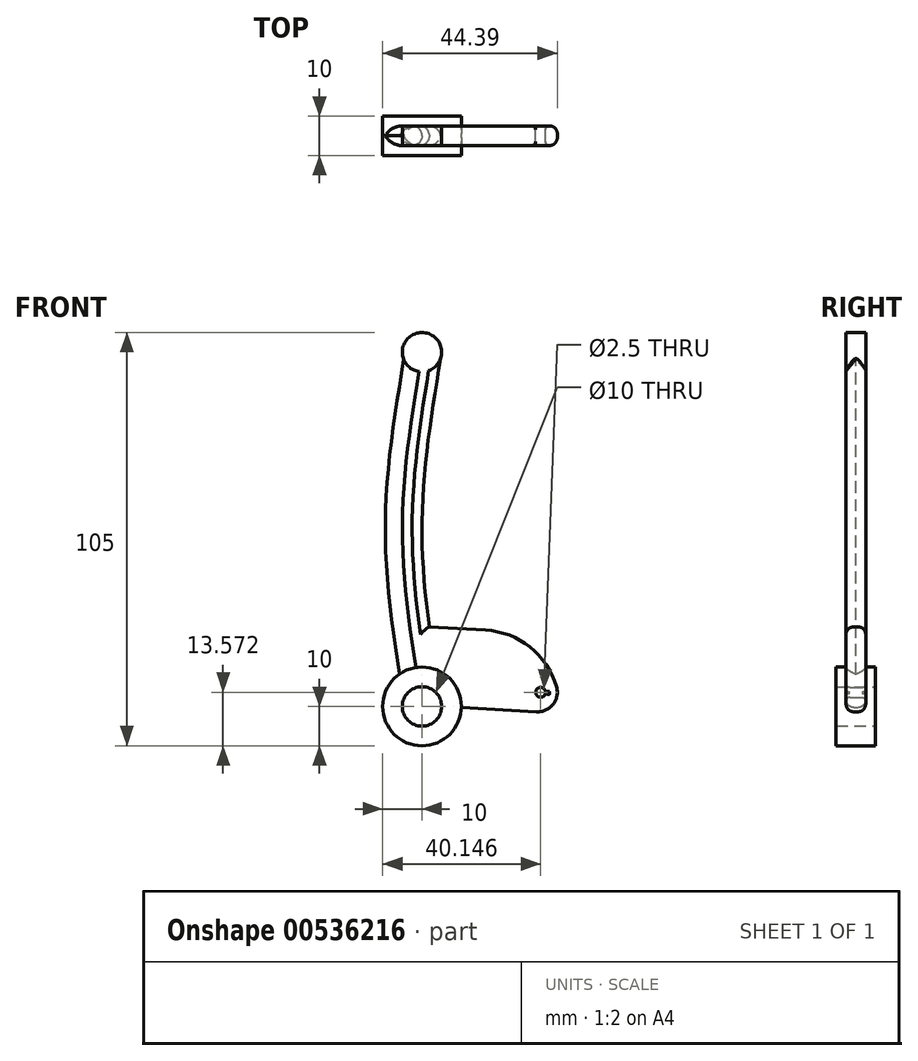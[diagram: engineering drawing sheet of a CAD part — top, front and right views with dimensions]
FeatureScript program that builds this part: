
annotation { "Feature Type Name" : "Feature", "Feature Type Description" : "" }
export const myFeature = defineFeature(function(context is Context, id is Id, definition is map)
    precondition{}
    {
        {
            var Q0;
            Q0=qCreatedBy(makeId("Front.planeOp"),FACE);
            var sketch = newSketch(context, id + "F0", { "sketchPlane" : qUnion([Q0])});
            skPoint(sketch, "E0.middle", {"position": v(0, 0) * mm});
            skFitSpline(sketch, "E1", {"points": [v(7.5, 45) * mm, v(2.5, 0) * mm, v(7.5, -45) * mm], "startDerivative": vector(-15, -90) * mm, "endDerivative": vector(15, -90) * mm});
            skFitSpline(sketch, "E2", {"points": [v(-2.5, -45) * mm, v(-7.5, 0) * mm, v(-2.5, 45) * mm], "startDerivative": vector(-15, 90) * mm, "endDerivative": vector(15, 90) * mm});
            skPoint(sketch, "E3.start.orphan", {"position": v(7.5, 0) * mm});
            skCircle(sketch, "E4", {"center": v(2.5, -45) * mm, "radius": 10 * mm});
            skCircle(sketch, "E5", {"center": v(2.5, -45) * mm, "radius": 5 * mm});
            skArc(sketch, "E6", {"start": v(7.23, 43.38) * mm, "mid": v(3.32, 49.93) * mm, "end": v(-2.5, 45) * mm});
            skLineSegment(sketch, "E7", {"start": v(7.5, -45) * mm, "end": v(37.45, -46.7) * mm});
            skLineSegment(sketch, "E8", {"start": v(37.45, -46.7) * mm, "end": v(38.59, -26.73) * mm});
            skLineSegment(sketch, "E9", {"start": v(38.59, -26.73) * mm, "end": v(4.36, -24.79) * mm});
            skCircle(sketch, "E10", {"center": v(32.65, -41.43) * mm, "radius": 1.25 * mm});
            skSolve(sketch);
        }
        {
            var Q0;
            Q0 = qSketchRegion(id + "F0", true);
            extrude(context, id + "F1", {"entities" : qUnion([Q0]), "depth" : 5 * mm, "offsetDistance" : 25 * mm, "symmetric" : true});
        }
        {
            var Q0;
            Q0=makeQuery(id+"F1.opExtrude","CAP_EDGE",EDGE,{"disambiguationData":[OSD([sQuery(id+"F0.wireOp",EDGE,"E2")])],"isStart":false});
            var Q1;
            Q1=makeQuery(id+"F1.opExtrude","CAP_EDGE",EDGE,{"disambiguationData":[OSD([sQuery(id+"F0.wireOp",EDGE,"E2")])],"isStart":true});
            fillet(context, id + "F2", {"entities" : qUnion([Q0, Q1]), "radius" : 5 * mm, "tangentPropagation" : true, "allowEdgeOverflow" : false});
        }
        {
            var Q0;
            Q0=makeQuery(id+"F1.opExtrude","CAP_EDGE",EDGE,{"disambiguationData":[OSD([sQuery(id+"F0.wireOp",EDGE,"E1")])],"isStart":false});
            var Q1;
            Q1=makeQuery(id+"F1.opExtrude","CAP_EDGE",EDGE,{"disambiguationData":[OSD([sQuery(id+"F0.wireOp",EDGE,"E1")])],"isStart":true});
            fillet(context, id + "F3", {"entities" : qUnion([Q0, Q1]), "radius" : 2.5 * mm, "tangentPropagation" : true, "allowEdgeOverflow" : false});
        }
        {
            var Q0;
            Q0=makeQuery(id+"F1.opExtrude","CAP_FACE",FACE,{"disambiguationData":[OSD([sQuery(id+"F0.wireOp",EDGE,"E1"),sQuery(id+"F0.wireOp",EDGE,"E2"),sQuery(id+"F0.wireOp",EDGE,"E4"),sQuery(id+"F0.wireOp",EDGE,"E5"),sQuery(id+"F0.wireOp",EDGE,"E6")])],"isStart":false});
            var sketch = newSketch(context, id + "F4", { "sketchPlane" : qUnion([Q0])});
            skCircle(sketch, "E11", {"center": v(2.5, -45) * mm, "radius": 10 * mm});
            skSolve(sketch);
        }
        {
            var Q0;
            Q0 = qSketchRegion(id + "F4", true);
            extrude(context, id + "F5", {"entities" : qUnion([Q0]), "operationType" : NewBodyOperationType.ADD, "depth" : 2.5 * mm, "offsetDistance" : 25 * mm});
        }
        {
            var Q0;
            Q0=makeQuery(id+"F5.opExtrude","CAP_FACE",FACE,{"disambiguationData":[OSD([sQuery(id+"F4.wireOp",EDGE,"E11")])],"isStart":true});
            extrude(context, id + "F6", {"entities" : qUnion([Q0]), "operationType" : NewBodyOperationType.REMOVE, "oppositeDirection" : true, "depth" : 25 * mm, "offsetDistance" : 25 * mm});
        }
        {
            var Q0;
            Q0=makeQuery(id+"F5.opExtrude","CAP_FACE",FACE,{"disambiguationData":[OSD([sQuery(id+"F4.wireOp",EDGE,"E11")])],"isStart":false});
            extrude(context, id + "F7", {"entities" : qUnion([Q0]), "operationType" : NewBodyOperationType.ADD, "oppositeDirection" : true, "depth" : 10 * mm, "offsetDistance" : 25 * mm});
        }
        {
            var Q0;
            Q0=makeQuery(id+"F1.opExtrude","SWEPT_EDGE",EDGE,{"disambiguationData":[OSD([sQuery(id+"F0.wireOp",EDGE,"E8"),sQuery(id+"F0.wireOp",EDGE,"E9")])]});
            fillet(context, id + "F8", {"entities" : qUnion([Q0]), "radius" : 20 * mm, "tangentPropagation" : true, "allowEdgeOverflow" : false});
        }
        {
            var Q0;
            Q0=makeQuery(id+"F8.opFillet","BLEND_EDGE",EDGE,{"blendedFrom":[makeQuery(id+"F1.opExtrude","SWEPT_EDGE",EDGE,{"disambiguationData":[OSD([sQuery(id+"F0.wireOp",EDGE,"E8"),sQuery(id+"F0.wireOp",EDGE,"E9")])]}),makeQuery(id+"F1.opExtrude","SWEPT_FACE",FACE,{"disambiguationData":[OSD([sQuery(id+"F0.wireOp",EDGE,"E7")])]})],"blendedInto":[makeQuery(id+"F1.opExtrude","SWEPT_FACE",FACE,{"disambiguationData":[OSD([sQuery(id+"F0.wireOp",EDGE,"E7")])]})]});
            fillet(context, id + "F9", {"entities" : qUnion([Q0]), "radius" : 5 * mm, "tangentPropagation" : true, "allowEdgeOverflow" : false});
        }
        {
            var Q0;
            {var subQ0=sQuery(id+"F0.wireOp",EDGE,"E9");var subQ1=sQuery(id+"F0.wireOp",EDGE,"E8");Q0=makeQuery(id+"F8.opFillet","BLEND_EDGE",EDGE,{"blendedFrom":[makeQuery(id+"F1.opExtrude","SWEPT_EDGE",EDGE,{"disambiguationData":[OSD([subQ1,subQ0])]}),makeQuery(id+"F1.opExtrude","CAP_FACE",FACE,{"disambiguationData":[OSD([sQuery(id+"F0.wireOp",EDGE,"E1"),sQuery(id+"F0.wireOp",EDGE,"E2"),sQuery(id+"F0.wireOp",EDGE,"E4"),sQuery(id+"F0.wireOp",EDGE,"E5"),sQuery(id+"F0.wireOp",EDGE,"E6"),sQuery(id+"F0.wireOp",EDGE,"E7"),subQ1,subQ0])],"isStart":true})],"blendedInto":[makeQuery(id+"F1.opExtrude","CAP_FACE",FACE,{"disambiguationData":[OSD([sQuery(id+"F0.wireOp",EDGE,"E1"),sQuery(id+"F0.wireOp",EDGE,"E2"),sQuery(id+"F0.wireOp",EDGE,"E4"),sQuery(id+"F0.wireOp",EDGE,"E5"),sQuery(id+"F0.wireOp",EDGE,"E6"),sQuery(id+"F0.wireOp",EDGE,"E7"),subQ1,subQ0])],"isStart":true})]});}
            var Q1;
            {var subQ0=sQuery(id+"F0.wireOp",EDGE,"E9");var subQ1=sQuery(id+"F0.wireOp",EDGE,"E8");Q1=makeQuery(id+"F8.opFillet","BLEND_EDGE",EDGE,{"blendedFrom":[makeQuery(id+"F1.opExtrude","SWEPT_EDGE",EDGE,{"disambiguationData":[OSD([subQ1,subQ0])]}),makeQuery(id+"F1.opExtrude","CAP_FACE",FACE,{"disambiguationData":[OSD([sQuery(id+"F0.wireOp",EDGE,"E1"),sQuery(id+"F0.wireOp",EDGE,"E2"),sQuery(id+"F0.wireOp",EDGE,"E4"),sQuery(id+"F0.wireOp",EDGE,"E5"),sQuery(id+"F0.wireOp",EDGE,"E6"),sQuery(id+"F0.wireOp",EDGE,"E7"),subQ1,subQ0])],"isStart":false})],"blendedInto":[makeQuery(id+"F1.opExtrude","CAP_FACE",FACE,{"disambiguationData":[OSD([sQuery(id+"F0.wireOp",EDGE,"E1"),sQuery(id+"F0.wireOp",EDGE,"E2"),sQuery(id+"F0.wireOp",EDGE,"E4"),sQuery(id+"F0.wireOp",EDGE,"E5"),sQuery(id+"F0.wireOp",EDGE,"E6"),sQuery(id+"F0.wireOp",EDGE,"E7"),subQ1,subQ0])],"isStart":false})]});}
            fillet(context, id + "F10", {"entities" : qUnion([Q0, Q1]), "radius" : 2 * mm, "tangentPropagation" : true, "allowEdgeOverflow" : false});
        }
        {
            var Q0;
            Q0=makeQuery(id+"F1.opExtrude","CAP_EDGE",EDGE,{"disambiguationData":[OSD([sQuery(id+"F0.wireOp",EDGE,"E10")])],"isStart":false});
            var Q1;
            Q1=makeQuery(id+"F1.opExtrude","CAP_EDGE",EDGE,{"disambiguationData":[OSD([sQuery(id+"F0.wireOp",EDGE,"E10")])],"isStart":true});
            fillet(context, id + "F11", {"entities" : qUnion([Q0, Q1]), "radius" : 1 * mm, "tangentPropagation" : true, "allowEdgeOverflow" : false});
        }
    });
